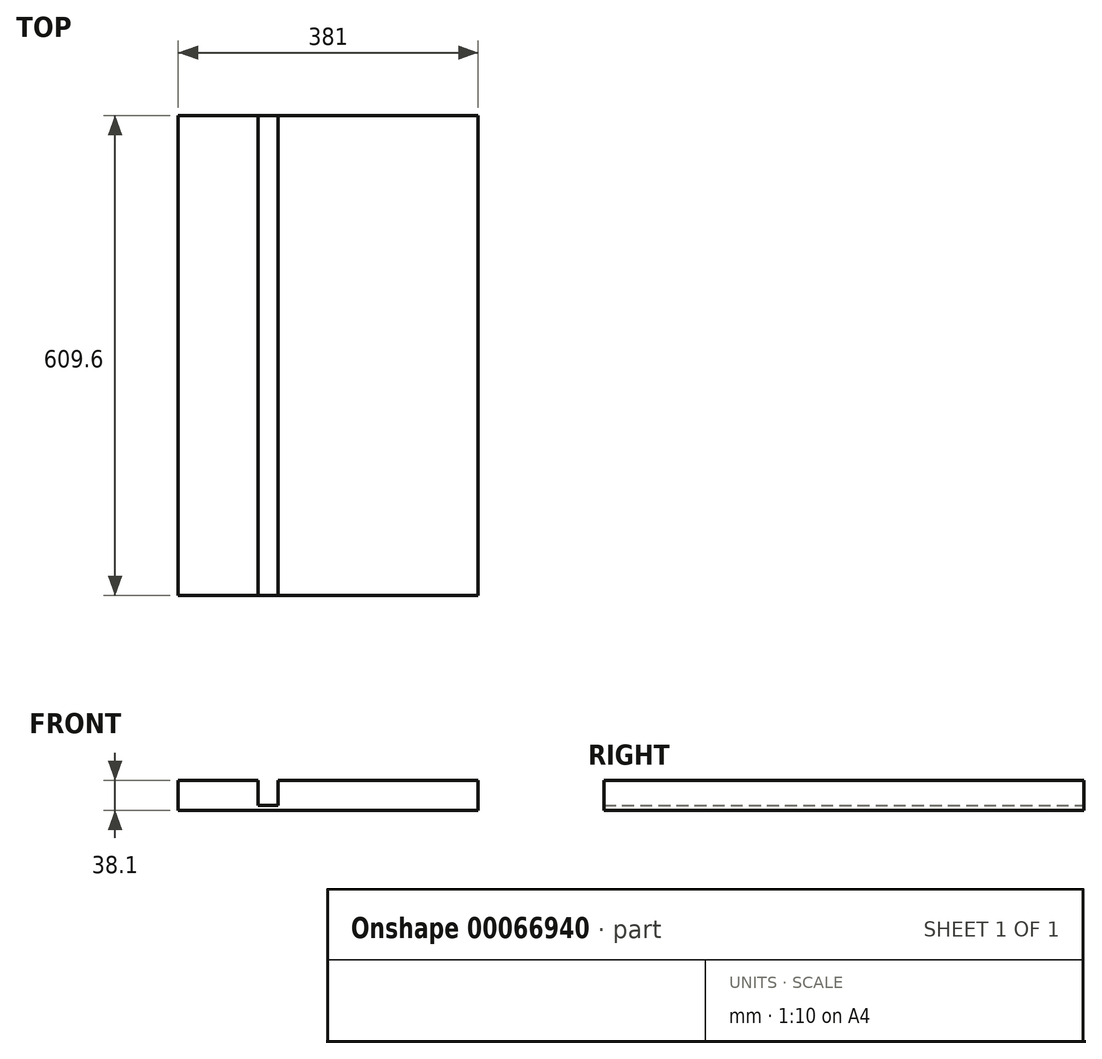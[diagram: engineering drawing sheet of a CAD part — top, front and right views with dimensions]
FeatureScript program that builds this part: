
annotation { "Feature Type Name" : "Feature", "Feature Type Description" : "" }
export const myFeature = defineFeature(function(context is Context, id is Id, definition is map)
    precondition{}
    {
        {
            var Q0;
            Q0=qCreatedBy(makeId("Front.planeOp"),FACE);
            var sketch = newSketch(context, id + "F0", { "sketchPlane" : qUnion([Q0])});
            skLineSegment(sketch, "E0", {"start": v(0, 0) * mm, "end": v(381, 0) * mm});
            skLineSegment(sketch, "E1", {"start": v(381, 38.1) * mm, "end": v(127, 38.1) * mm});
            skLineSegment(sketch, "E2", {"start": v(127, 38.1) * mm, "end": v(127, 6.35) * mm});
            skLineSegment(sketch, "E3", {"start": v(127, 6.35) * mm, "end": v(101.6, 6.35) * mm});
            skLineSegment(sketch, "E4", {"start": v(101.6, 6.35) * mm, "end": v(101.6, 38.1) * mm});
            skLineSegment(sketch, "E5", {"start": v(101.6, 38.1) * mm, "end": v(0, 38.1) * mm});
            skLineSegment(sketch, "E6", {"start": v(0, 38.1) * mm, "end": v(0, 0) * mm});
            skLineSegment(sketch, "E7", {"start": v(381, 0) * mm, "end": v(381, 38.1) * mm});
            skSolve(sketch);
        }
        {
            var Q0;
            Q0=makeQuery(id+"F0.imprint","IMPRINT",FACE,{"disambiguationData":[TD([[makeQuery(id+"F0.imprint","IMPRINT",EDGE,{"derivedFrom":sQuery(id+"F0.wireOp",EDGE,"E0")}),1.0]])]});
            extrude(context, id + "F1", {"entities" : qUnion([Q0]), "depth" : 609.6 * mm});
        }
    });
